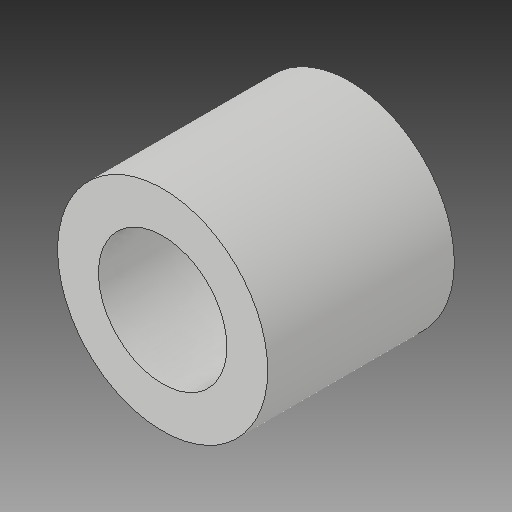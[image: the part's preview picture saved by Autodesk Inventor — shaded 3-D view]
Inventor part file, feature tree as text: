
AUTODESK INVENTOR PART (.ipt)
format: ipt  version: 2018 (Build 220112000, 112)  size: 103,936 bytes
history: native  units: mm
features: other x3, extrude x1, sketch x1, reference x1
ambient origin geometry x8: Origin, YZ Plane, XZ Plane, XY Plane, X Axis, Y Axis, Z Axis, Center Point
bodies: Solid1 (feature_tree)
feature tree (6):
  extrude  "Extrusion1"  Depth=8.0mm
  sketch  "Sketch1"  dims[d0=5.5mm d1=9.0mm d2=8.0mm d3=0.0mm]
  reference  "Reference1"
  parser-record x1  (decoder bookkeeping rows leaked as tree rows — omitted from the tree; the rows remain in map.json)
  other  "eLECTRONICS-ENCLOSURE.iam"
  other  "EE Base:1"
note: 1 file-system path scrubbed to <path> (originals preserved in map.json)
